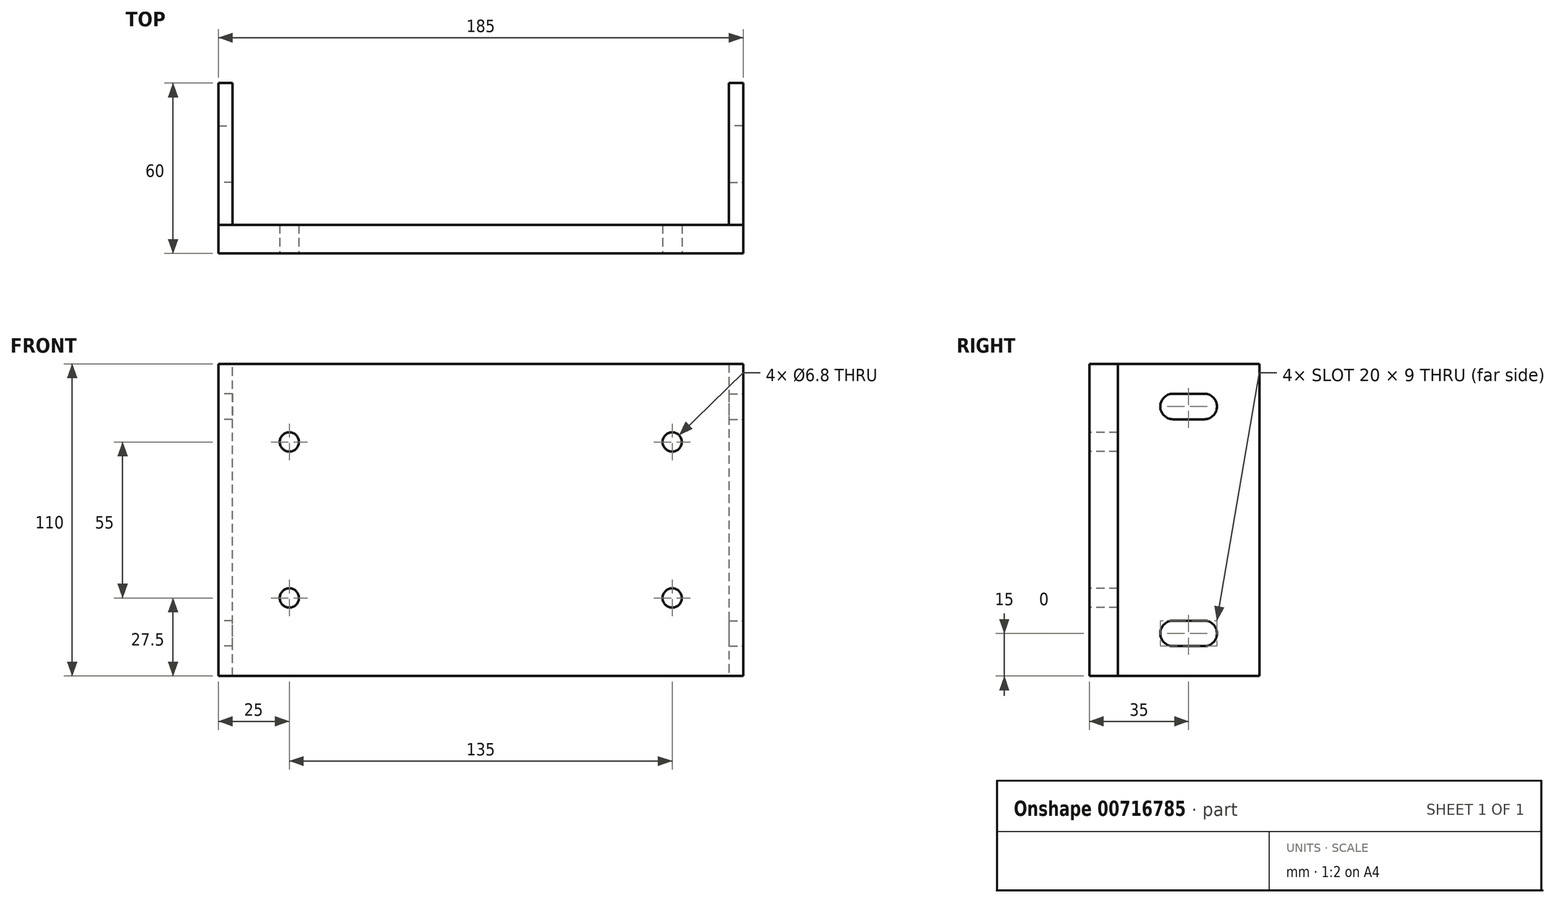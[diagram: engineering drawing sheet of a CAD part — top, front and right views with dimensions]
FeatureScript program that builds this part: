
annotation { "Feature Type Name" : "Feature", "Feature Type Description" : "" }
export const myFeature = defineFeature(function(context is Context, id is Id, definition is map)
    precondition{}
    {
        {
            var Q0;
            Q0=qCreatedBy(makeId("Front.planeOp"),FACE);
            var sketch = newSketch(context, id + "F0", { "sketchPlane" : qUnion([Q0])});
            skLineSegment(sketch, "E0.bottom", {"start": v(-92.5, -55) * mm, "end": v(92.5, -55) * mm});
            skLineSegment(sketch, "E0.top", {"start": v(-92.5, 55) * mm, "end": v(92.5, 55) * mm});
            skLineSegment(sketch, "E0.left", {"start": v(-92.5, -55) * mm, "end": v(-92.5, 55) * mm});
            skLineSegment(sketch, "E0.right", {"start": v(92.5, -55) * mm, "end": v(92.5, 55) * mm});
            skLineSegment(sketch, "E1", {"start": v(-92.5, 0) * mm, "end": v(92.5, 0) * mm, "construction": true});
            skSolve(sketch);
        }
        {
            var Q0;
            Q0 = qSketchRegion(id + "F0", true);
            extrude(context, id + "F1", {"entities" : qUnion([Q0]), "endBound" : BoundingType.SYMMETRIC, "depth" : 10 * mm, "offsetDistance" : 25 * mm});
        }
        {
            var Q0;
            Q0=makeQuery(id+"F1.opExtrude","CAP_FACE",FACE,{"disambiguationData":[OSD([sQuery(id+"F0.wireOp",EDGE,"E0.bottom"),sQuery(id+"F0.wireOp",EDGE,"E0.top"),sQuery(id+"F0.wireOp",EDGE,"E0.left"),sQuery(id+"F0.wireOp",EDGE,"E0.right")])],"isStart":false});
            var sketch = newSketch(context, id + "F2", { "sketchPlane" : qUnion([Q0])});
            skPoint(sketch, "E2", {"position": v(-67.5, 27.5) * mm});
            skPoint(sketch, "E3", {"position": v(67.5, 27.5) * mm});
            skPoint(sketch, "E4", {"position": v(67.5, -27.5) * mm});
            skPoint(sketch, "E5", {"position": v(-67.5, -27.5) * mm});
            skSolve(sketch);
        }
        {
            var Q0;
            Q0=sQuery(id+"F2.wireOp",VERTEX,"E2");
            var Q1;
            Q1=sQuery(id+"F2.wireOp",VERTEX,"E5");
            var Q2;
            Q2=sQuery(id+"F2.wireOp",VERTEX,"E4");
            var Q3;
            Q3=sQuery(id+"F2.wireOp",VERTEX,"E3");
            var Q4;
            Q4=makeQuery(id+"F1.opExtrude","SWEPT_BODY",BODY,{"disambiguationData":[OSD([sQuery(id+"F0.wireOp",EDGE,"E0.bottom"),sQuery(id+"F0.wireOp",EDGE,"E0.top"),sQuery(id+"F0.wireOp",EDGE,"E0.left"),sQuery(id+"F0.wireOp",EDGE,"E0.right")])]});
            hole(context, id + "F3", {"style" : HoleStyle.SIMPLE, "endStyle" : HoleEndStyle.THROUGH, "standardTappedOrClearance" : lookupTablePath({ "standard" : "ISO", "engagement" : "75%", "pitch" : "1.25 mm", "size" : "M8", "type" : "Tapped" }), "standardBlindInLast" : lookupTablePath({ "standard" : "ISO", "engagement" : "75%", "pitch" : "1.25 mm", "size" : "M8", "type" : "Tapped" }), "holeDiameter" : 6.8 * mm, "majorDiameter" : 8 * mm, "showTappedDepth" : true, "isTappedThrough" : true, "tappedDepth" : 12 * mm, "tapClearance" : 3, "startFromSketch" : true, "locations" : qUnion([Q0, Q1, Q2, Q3]), "scope" : qUnion([Q4])});
        }
        {
            var Q0;
            Q0=makeQuery(id+"F1.opExtrude","SWEPT_FACE",FACE,{"disambiguationData":[OSD([sQuery(id+"F0.wireOp",EDGE,"E0.right")])]});
            var sketch = newSketch(context, id + "F4", { "sketchPlane" : qUnion([Q0])});
            skLineSegment(sketch, "E6.bottom", {"start": v(5, 55) * mm, "end": v(55, 55) * mm});
            skLineSegment(sketch, "E6.top", {"start": v(5, -55) * mm, "end": v(55, -55) * mm});
            skLineSegment(sketch, "E6.left", {"start": v(5, 55) * mm, "end": v(5, -55) * mm});
            skLineSegment(sketch, "E6.right", {"start": v(55, 55) * mm, "end": v(55, -55) * mm});
            skSolve(sketch);
        }
        {
            var Q0;
            Q0 = qSketchRegion(id + "F4", true);
            extrude(context, id + "F5", {"entities" : qUnion([Q0]), "oppositeDirection" : true, "depth" : 5 * mm, "offsetDistance" : 25 * mm});
        }
        {
            var Q0;
            Q0=makeQuery(id+"F5.opExtrude","CAP_FACE",FACE,{"disambiguationData":[OSD([sQuery(id+"F4.wireOp",EDGE,"E6.bottom"),sQuery(id+"F4.wireOp",EDGE,"E6.top"),sQuery(id+"F4.wireOp",EDGE,"E6.left"),sQuery(id+"F4.wireOp",EDGE,"E6.right")])],"isStart":true});
            var sketch = newSketch(context, id + "F6", { "sketchPlane" : qUnion([Q0])});
            skLineSegment(sketch, "E7.bottom", {"start": v(20, 44.5) * mm, "end": v(40, 44.5) * mm});
            skLineSegment(sketch, "E7.top", {"start": v(20, 35.5) * mm, "end": v(40, 35.5) * mm});
            skLineSegment(sketch, "E7.left", {"start": v(20, 44.5) * mm, "end": v(20, 35.5) * mm});
            skLineSegment(sketch, "E7.right", {"start": v(40, 44.5) * mm, "end": v(40, 35.5) * mm});
            skLineSegment(sketch, "E8.bottom", {"start": v(20, -35.5) * mm, "end": v(40, -35.5) * mm});
            skLineSegment(sketch, "E8.top", {"start": v(20, -44.5) * mm, "end": v(40, -44.5) * mm});
            skLineSegment(sketch, "E8.left", {"start": v(20, -35.5) * mm, "end": v(20, -44.5) * mm});
            skLineSegment(sketch, "E8.right", {"start": v(40, -35.5) * mm, "end": v(40, -44.5) * mm});
            skLineSegment(sketch, "E9", {"start": v(30, 35.5) * mm, "end": v(30, -35.5) * mm, "construction": true});
            skLineSegment(sketch, "E10", {"start": v(30, 0) * mm, "end": v(55, 0) * mm, "construction": true});
            skSolve(sketch);
        }
        {
            var Q0;
            Q0 = qSketchRegion(id + "F6", true);
            extrude(context, id + "F7", {"entities" : qUnion([Q0]), "operationType" : NewBodyOperationType.REMOVE, "endBound" : BoundingType.THROUGH_ALL, "oppositeDirection" : true, "depth" : 25 * mm, "offsetDistance" : 25 * mm});
        }
        {
            var Q0;
            Q0=makeQuery(id+"F7.boolean.opBoolean","COPY",EDGE,{"derivedFrom":makeQuery(id+"F7.opExtrude","SWEPT_EDGE",EDGE,{"disambiguationData":[OSD([sQuery(id+"F6.wireOp",EDGE,"E7.top"),sQuery(id+"F6.wireOp",EDGE,"E7.left")])]})});
            var Q1;
            Q1=makeQuery(id+"F7.boolean.opBoolean","COPY",EDGE,{"derivedFrom":makeQuery(id+"F7.opExtrude","SWEPT_EDGE",EDGE,{"disambiguationData":[OSD([sQuery(id+"F6.wireOp",EDGE,"E7.bottom"),sQuery(id+"F6.wireOp",EDGE,"E7.left")])]})});
            var Q2;
            Q2=makeQuery(id+"F7.boolean.opBoolean","COPY",EDGE,{"derivedFrom":makeQuery(id+"F7.opExtrude","SWEPT_EDGE",EDGE,{"disambiguationData":[OSD([sQuery(id+"F6.wireOp",EDGE,"E8.bottom"),sQuery(id+"F6.wireOp",EDGE,"E8.left")])]})});
            var Q3;
            Q3=makeQuery(id+"F7.boolean.opBoolean","COPY",EDGE,{"derivedFrom":makeQuery(id+"F7.opExtrude","SWEPT_EDGE",EDGE,{"disambiguationData":[OSD([sQuery(id+"F6.wireOp",EDGE,"E8.top"),sQuery(id+"F6.wireOp",EDGE,"E8.left")])]})});
            var Q4;
            Q4=makeQuery(id+"F7.boolean.opBoolean","COPY",EDGE,{"derivedFrom":makeQuery(id+"F7.opExtrude","SWEPT_EDGE",EDGE,{"disambiguationData":[OSD([sQuery(id+"F6.wireOp",EDGE,"E8.bottom"),sQuery(id+"F6.wireOp",EDGE,"E8.right")])]})});
            var Q5;
            Q5=makeQuery(id+"F7.boolean.opBoolean","COPY",EDGE,{"derivedFrom":makeQuery(id+"F7.opExtrude","SWEPT_EDGE",EDGE,{"disambiguationData":[OSD([sQuery(id+"F6.wireOp",EDGE,"E7.bottom"),sQuery(id+"F6.wireOp",EDGE,"E7.right")])]})});
            var Q6;
            Q6=makeQuery(id+"F7.boolean.opBoolean","COPY",EDGE,{"derivedFrom":makeQuery(id+"F7.opExtrude","SWEPT_EDGE",EDGE,{"disambiguationData":[OSD([sQuery(id+"F6.wireOp",EDGE,"E7.top"),sQuery(id+"F6.wireOp",EDGE,"E7.right")])]})});
            var Q7;
            Q7=makeQuery(id+"F7.boolean.opBoolean","COPY",EDGE,{"derivedFrom":makeQuery(id+"F7.opExtrude","SWEPT_EDGE",EDGE,{"disambiguationData":[OSD([sQuery(id+"F6.wireOp",EDGE,"E8.top"),sQuery(id+"F6.wireOp",EDGE,"E8.right")])]})});
            fillet(context, id + "F8", {"entities" : qUnion([Q0, Q1, Q2, Q3, Q4, Q5, Q6, Q7]), "radius" : 4.5 * mm, "tangentPropagation" : true, "allowEdgeOverflow" : false});
        }
        {
            var Q0;
            Q0=makeQuery(id+"F5.opExtrude","SWEPT_BODY",BODY,{"disambiguationData":[OSD([sQuery(id+"F4.wireOp",EDGE,"E6.bottom"),sQuery(id+"F4.wireOp",EDGE,"E6.top"),sQuery(id+"F4.wireOp",EDGE,"E6.left"),sQuery(id+"F4.wireOp",EDGE,"E6.right")])]});
            var Q1;
            Q1=qCreatedBy(makeId("Right.planeOp"),FACE);
            mirror(context, id + "F9", {"entities" : qUnion([Q0]), "mirrorPlane" : qUnion([Q1])});
        }
    });
